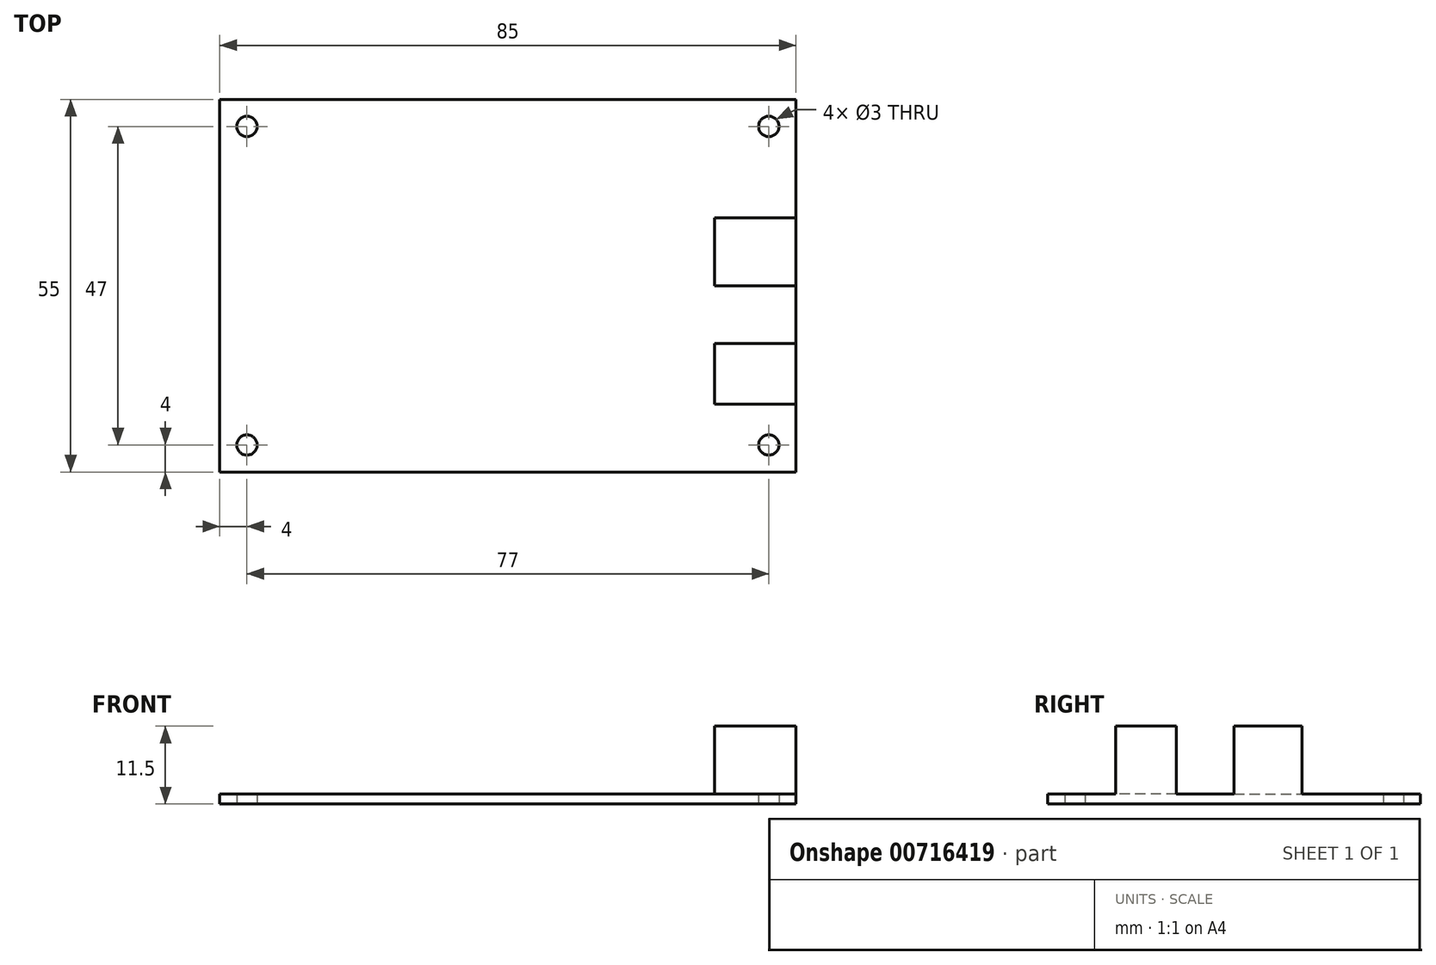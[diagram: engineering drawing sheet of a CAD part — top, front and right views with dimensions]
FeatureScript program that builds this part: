
annotation { "Feature Type Name" : "Feature", "Feature Type Description" : "" }
export const myFeature = defineFeature(function(context is Context, id is Id, definition is map)
    precondition{}
    {
        {
            var Q0;
            Q0=qCreatedBy(makeId("Top.planeOp"),FACE);
            var sketch = newSketch(context, id + "F0", { "sketchPlane" : qUnion([Q0])});
            skLineSegment(sketch, "E0.bottom", {"start": v(0, 0) * mm, "end": v(85, 0) * mm});
            skLineSegment(sketch, "E0.top", {"start": v(0, 55) * mm, "end": v(85, 55) * mm});
            skLineSegment(sketch, "E0.left", {"start": v(0, 0) * mm, "end": v(0, 55) * mm});
            skLineSegment(sketch, "E0.right", {"start": v(85, 0) * mm, "end": v(85, 55) * mm});
            skLineSegment(sketch, "E1", {"start": v(42.5, 55) * mm, "end": v(42.5, 0) * mm, "construction": true});
            skLineSegment(sketch, "E2", {"start": v(0, 27.5) * mm, "end": v(85, 27.5) * mm, "construction": true});
            skCircle(sketch, "E3", {"center": v(4, 4) * mm, "radius": 1.5 * mm});
            skCircle(sketch, "E4.MirrorC", {"center": v(4, 51) * mm, "radius": 1.5 * mm});
            skCircle(sketch, "E5.MirrorC", {"center": v(81, 51) * mm, "radius": 1.5 * mm});
            skCircle(sketch, "E6.MirrorC", {"center": v(81, 4) * mm, "radius": 1.5 * mm});
            skSolve(sketch);
        }
        {
            var Q0;
            Q0 = qSketchRegion(id + "F0", true);
            extrude(context, id + "F1", {"entities" : qUnion([Q0]), "depth" : 1.5 * mm, "offsetDistance" : 25 * mm});
        }
        {
            var Q0;
            Q0=makeQuery(id+"F1.opExtrude","CAP_FACE",FACE,{"disambiguationData":[OSD([sQuery(id+"F0.wireOp",EDGE,"E0.bottom"),sQuery(id+"F0.wireOp",EDGE,"E0.top"),sQuery(id+"F0.wireOp",EDGE,"E0.left"),sQuery(id+"F0.wireOp",EDGE,"E0.right"),sQuery(id+"F0.wireOp",EDGE,"E3"),sQuery(id+"F0.wireOp",EDGE,"E4.MirrorC"),sQuery(id+"F0.wireOp",EDGE,"E5.MirrorC"),sQuery(id+"F0.wireOp",EDGE,"E6.MirrorC")])],"isStart":false});
            var sketch = newSketch(context, id + "F2", { "sketchPlane" : qUnion([Q0])});
            skLineSegment(sketch, "E7.bottom", {"start": v(73, 19) * mm, "end": v(85, 19) * mm});
            skLineSegment(sketch, "E7.top", {"start": v(73, 10) * mm, "end": v(85, 10) * mm});
            skLineSegment(sketch, "E7.left", {"start": v(73, 19) * mm, "end": v(73, 10) * mm});
            skLineSegment(sketch, "E7.right", {"start": v(85, 19) * mm, "end": v(85, 10) * mm});
            skPoint(sketch, "E8.firstSnap0", {"position": v(85, 27.5) * mm});
            skLineSegment(sketch, "E8.bottom", {"start": v(73, 27.5) * mm, "end": v(85, 27.5) * mm});
            skLineSegment(sketch, "E8.top", {"start": v(73, 37.5) * mm, "end": v(85, 37.5) * mm});
            skLineSegment(sketch, "E8.left", {"start": v(73, 27.5) * mm, "end": v(73, 37.5) * mm});
            skLineSegment(sketch, "E8.right", {"start": v(85, 27.5) * mm, "end": v(85, 37.5) * mm});
            skSolve(sketch);
        }
        {
            var Q0;
            Q0 = qSketchRegion(id + "F2", true);
            extrude(context, id + "F3", {"entities" : qUnion([Q0]), "operationType" : NewBodyOperationType.ADD, "depth" : 10 * mm, "offsetDistance" : 25 * mm});
        }
    });
